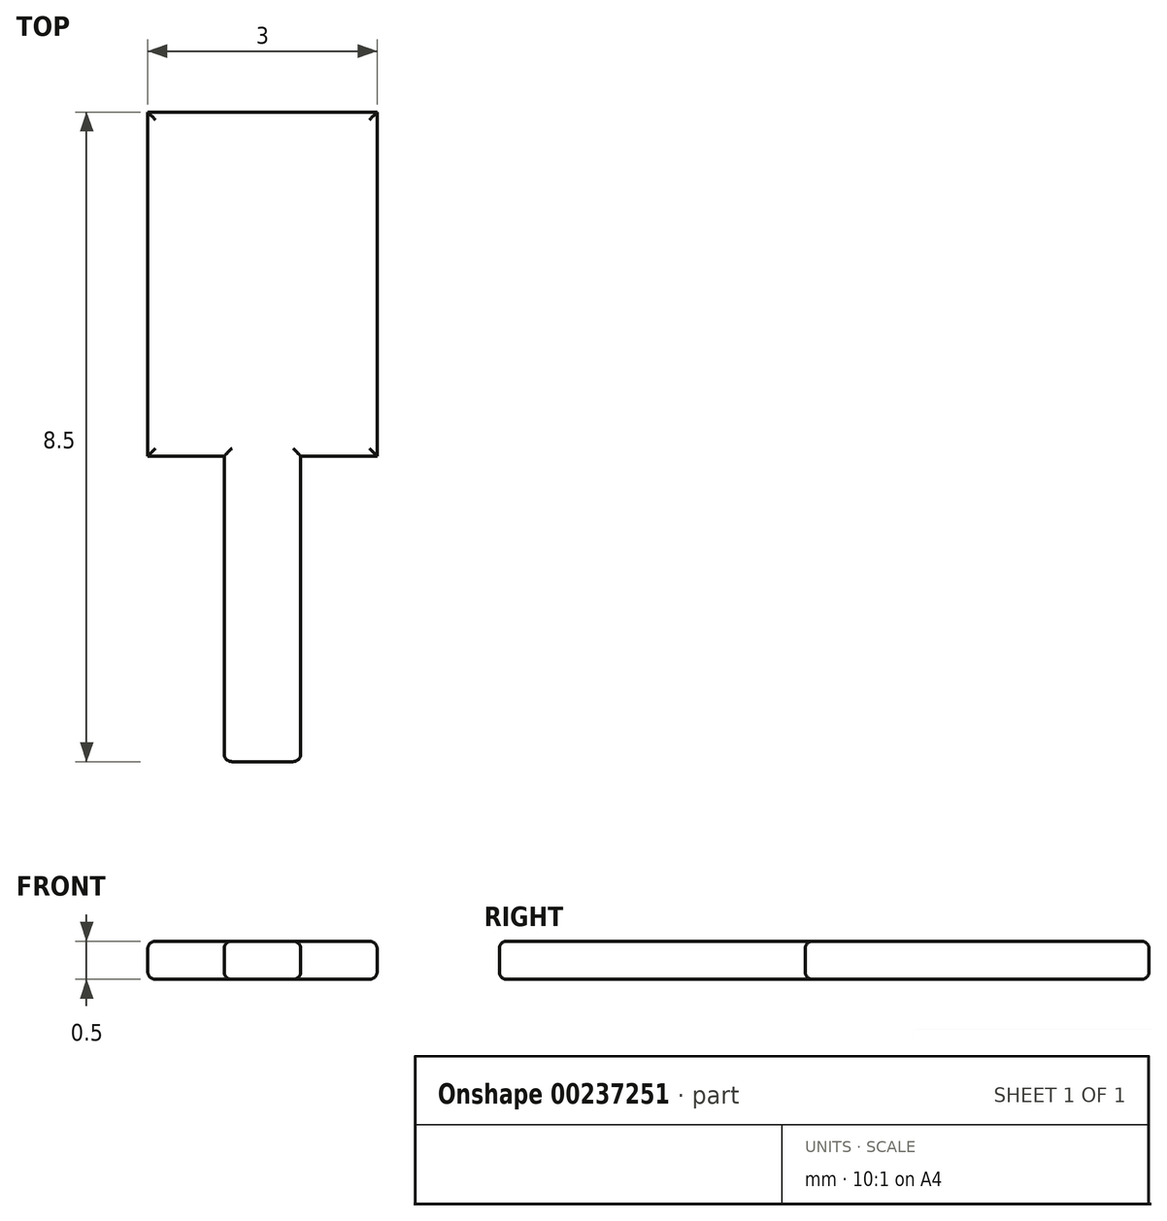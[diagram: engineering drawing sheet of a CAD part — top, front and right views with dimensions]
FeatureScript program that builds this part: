
annotation { "Feature Type Name" : "Feature", "Feature Type Description" : "" }
export const myFeature = defineFeature(function(context is Context, id is Id, definition is map)
    precondition{}
    {
        {
            var Q0;
            Q0=qCreatedBy(makeId("Top.planeOp"),FACE);
            var sketch = newSketch(context, id + "F0", { "sketchPlane" : qUnion([Q0])});
            skLineSegment(sketch, "E0.bottom", {"start": v(1.5, -2.25) * mm, "end": v(-1.5, -2.25) * mm});
            skLineSegment(sketch, "E0.top", {"start": v(1.5, 2.25) * mm, "end": v(-1.5, 2.25) * mm});
            skLineSegment(sketch, "E0.left", {"start": v(1.5, -2.25) * mm, "end": v(1.5, 2.25) * mm});
            skLineSegment(sketch, "E0.right", {"start": v(-1.5, -2.25) * mm, "end": v(-1.5, 2.25) * mm});
            skPoint(sketch, "E0.middle", {"position": v(0, 0) * mm});
            skSolve(sketch);
        }
        {
            var Q0;
            Q0 = qSketchRegion(id + "F0", true);
            extrude(context, id + "F1", {"entities" : qUnion([Q0]), "oppositeDirection" : true, "depth" : .5 * mm});
        }
        {
            var Q0;
            Q0=qCreatedBy(makeId("Front.planeOp"),FACE);
            cPlane(context, id + "F2", {"entities" : qUnion([Q0]), "cplaneType" : CPlaneType.OFFSET, "offset" : 2.25 * mm, "width" : 150 * mm, "height" : 150 * mm});
        }
        {
            var Q0;
            Q0=qCreatedBy(id+"F2.planeOp",FACE);
            var sketch = newSketch(context, id + "F3", { "sketchPlane" : qUnion([Q0])});
            skLineSegment(sketch, "E1.bottom", {"start": v(0.5, -3) * mm, "end": v(-0.5, -3) * mm});
            skLineSegment(sketch, "E1.top", {"start": v(0.5, 3) * mm, "end": v(-0.5, 3) * mm});
            skLineSegment(sketch, "E1.left", {"start": v(0.5, -3) * mm, "end": v(0.5, 3) * mm});
            skLineSegment(sketch, "E1.right", {"start": v(-0.5, -3) * mm, "end": v(-0.5, 3) * mm});
            skPoint(sketch, "E1.middle", {"position": v(0, 0) * mm});
            skSolve(sketch);
        }
        {
            var Q0;
            Q0=makeQuery(id+"F3.imprint","IMPRINT",FACE,{"disambiguationData":[TD([[makeQuery(id+"F3.imprint","IMPRINT",EDGE,{"derivedFrom":sQuery(id+"F3.wireOp",EDGE,"E1.bottom")}),-1.0]])]});
            extrude(context, id + "F4", {"entities" : qUnion([Q0]), "oppositeDirection" : true, "depth" : .5 * mm});
        }
        {
            var Q0;
            Q0=makeQuery(id+"F4.opExtrude","CAP_EDGE",EDGE,{"disambiguationData":[OSD([sQuery(id+"F3.wireOp",EDGE,"E1.bottom")])],"isStart":true});
            cPoint(context, id + "F5", {"entities" : qUnion([Q0]), "parameter" : 0.5});
        }
        {
            var Q0;
            Q0=makeQuery(id+"F4.opExtrude","SWEPT_BODY",BODY,{"disambiguationData":[OSD([sQuery(id+"F3.wireOp",EDGE,"E1.bottom"),sQuery(id+"F3.wireOp",EDGE,"E1.top"),sQuery(id+"F3.wireOp",EDGE,"E1.left"),sQuery(id+"F3.wireOp",EDGE,"E1.right")])]});
            var Q1;
            Q1=makeQuery(id+"F1.opExtrude","CAP_EDGE",EDGE,{"disambiguationData":[OSD([sQuery(id+"F0.wireOp",EDGE,"E0.bottom")])],"isStart":true});
            var Q2;
            Q2 = qCreatedBy(id + "F5" ,VERTEX);
            transform(context, id + "F6", {"entities" : qUnion([Q0]), "transformType" : TransformType.ROTATION, "transformAxis" : qUnion([Q1]), "angle" : 90 * degree, "makeCopy" : false});
        }
        {
            var Q0;
            Q0=makeQuery(id+"F4.opExtrude","SWEPT_BODY",BODY,{"disambiguationData":[OSD([sQuery(id+"F3.wireOp",EDGE,"E1.bottom"),sQuery(id+"F3.wireOp",EDGE,"E1.top"),sQuery(id+"F3.wireOp",EDGE,"E1.left"),sQuery(id+"F3.wireOp",EDGE,"E1.right")])]});
            transform(context, id + "F7", {"entities" : qUnion([Q0]), "transformType" : TransformType.TRANSLATION_3D, "dx" : 0 * mm, "dy" : -1 * mm, "dz" : 0 * mm, "makeCopy" : false});
        }
        {
            var Q0;
            Q0=makeQuery(id+"F1.opExtrude","SWEPT_BODY",BODY,{"disambiguationData":[OSD([sQuery(id+"F0.wireOp",EDGE,"E0.bottom"),sQuery(id+"F0.wireOp",EDGE,"E0.top"),sQuery(id+"F0.wireOp",EDGE,"E0.left"),sQuery(id+"F0.wireOp",EDGE,"E0.right")])]});
            var Q1;
            Q1=makeQuery(id+"F4.opExtrude","SWEPT_BODY",BODY,{"disambiguationData":[OSD([sQuery(id+"F3.wireOp",EDGE,"E1.bottom"),sQuery(id+"F3.wireOp",EDGE,"E1.top"),sQuery(id+"F3.wireOp",EDGE,"E1.left"),sQuery(id+"F3.wireOp",EDGE,"E1.right")])]});
            booleanBodies(context, id + "F8", {"operationType" : BooleanOperationType.UNION, "tools" : qUnion([Q0, Q1])});
        }
        {
            var Q0;
            Q0=makeQuery(id+"F8.opBoolean","MERGE",FACE,{"derivedFrom":[makeQuery(id+"F1.opExtrude","SWEPT_FACE",FACE,{"disambiguationData":[OSD([sQuery(id+"F0.wireOp",EDGE,"E0.bottom")])]}),makeQuery(id+"F4.opExtrude","CAP_FACE",FACE,{"disambiguationData":[OSD([sQuery(id+"F3.wireOp",EDGE,"E1.bottom"),sQuery(id+"F3.wireOp",EDGE,"E1.top"),sQuery(id+"F3.wireOp",EDGE,"E1.left"),sQuery(id+"F3.wireOp",EDGE,"E1.right")])],"isStart":true})]});
            fillet(context, id + "F9", {"entities" : qUnion([Q0]), "radius" : .1 * mm, "tangentPropagation" : true, "allowEdgeOverflow" : false});
        }
        {
            var Q0;
            Q0=makeQuery(id+"F1.opExtrude","CAP_FACE",FACE,{"disambiguationData":[OSD([sQuery(id+"F0.wireOp",EDGE,"E0.bottom"),sQuery(id+"F0.wireOp",EDGE,"E0.top"),sQuery(id+"F0.wireOp",EDGE,"E0.left"),sQuery(id+"F0.wireOp",EDGE,"E0.right")])],"isStart":false});
            fillet(context, id + "F10", {"entities" : qUnion([Q0]), "radius" : .1 * mm, "tangentPropagation" : true, "allowEdgeOverflow" : false});
        }
        {
            var Q0;
            Q0=makeQuery(id+"F4.opExtrude","CAP_FACE",FACE,{"disambiguationData":[OSD([sQuery(id+"F3.wireOp",EDGE,"E1.bottom"),sQuery(id+"F3.wireOp",EDGE,"E1.top"),sQuery(id+"F3.wireOp",EDGE,"E1.left"),sQuery(id+"F3.wireOp",EDGE,"E1.right")])],"isStart":false});
            var Q1;
            Q1=makeQuery(id+"F1.opExtrude","CAP_FACE",FACE,{"disambiguationData":[OSD([sQuery(id+"F0.wireOp",EDGE,"E0.bottom"),sQuery(id+"F0.wireOp",EDGE,"E0.top"),sQuery(id+"F0.wireOp",EDGE,"E0.left"),sQuery(id+"F0.wireOp",EDGE,"E0.right")])],"isStart":true});
            var Q2;
            Q2=makeQuery(id+"F4.opExtrude","SWEPT_FACE",FACE,{"disambiguationData":[OSD([sQuery(id+"F3.wireOp",EDGE,"E1.bottom")])]});
            fillet(context, id + "F11", {"entities" : qUnion([Q0, Q1, Q2]), "radius" : .1 * mm, "tangentPropagation" : true, "allowEdgeOverflow" : false});
        }
    });
